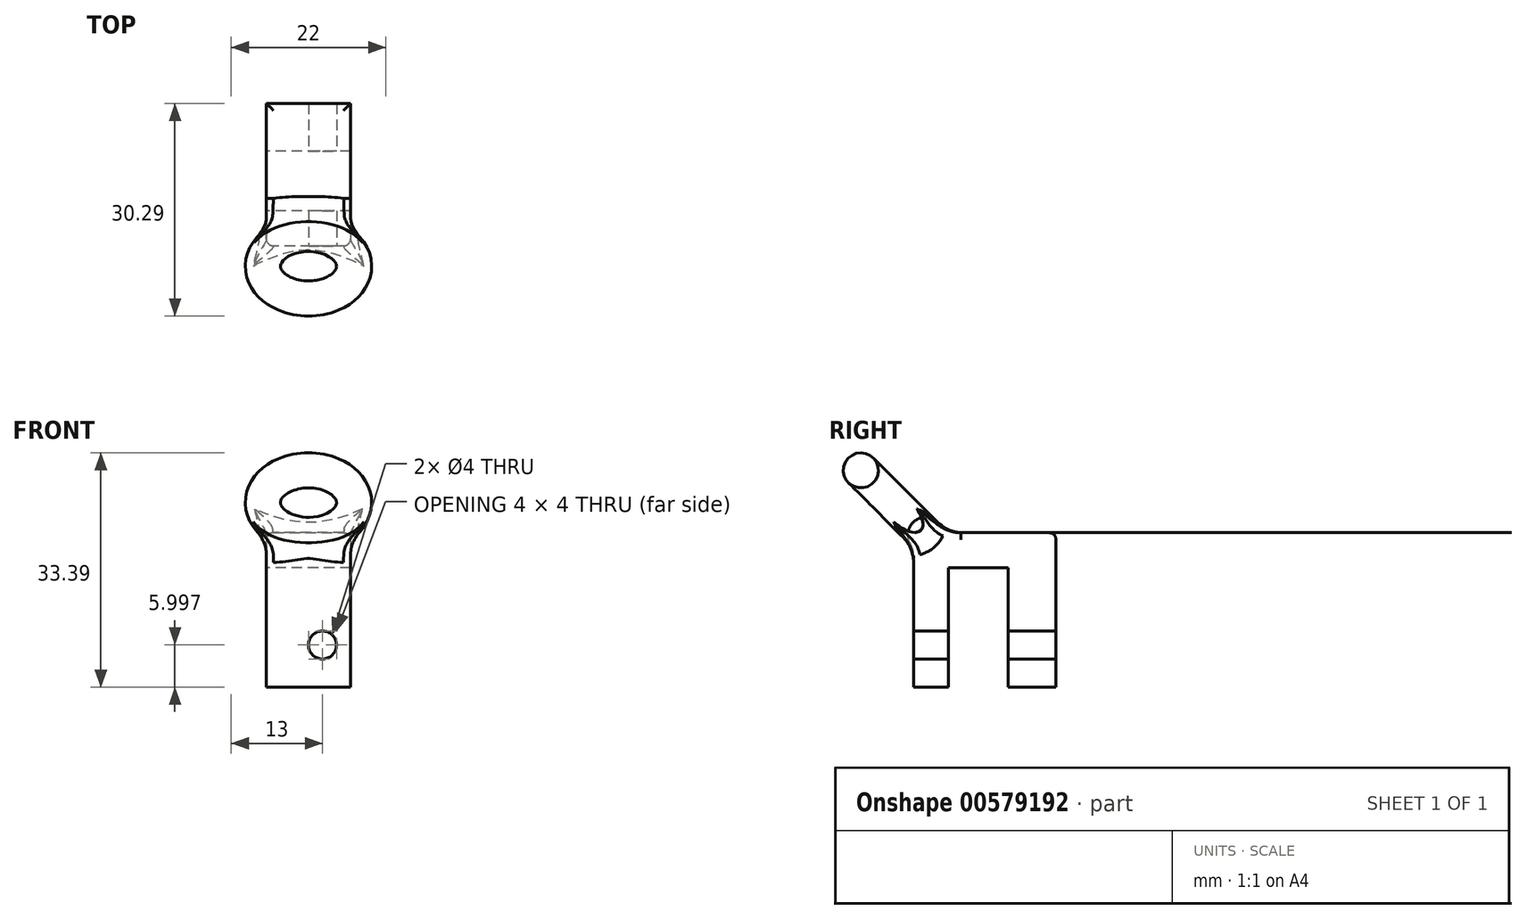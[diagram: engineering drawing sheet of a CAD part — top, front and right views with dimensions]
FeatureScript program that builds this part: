
annotation { "Feature Type Name" : "Feature", "Feature Type Description" : "" }
export const myFeature = defineFeature(function(context is Context, id is Id, definition is map)
    precondition{}
    {
        {
            var Q0;
            Q0=qCreatedBy(makeId("Right.planeOp"),FACE);
            var sketch = newSketch(context, id + "F0", { "sketchPlane" : qUnion([Q0])});
            skLineSegment(sketch, "E0", {"start": v(-9.26, -3.55) * mm, "end": v(-9.26, 18.45) * mm});
            skLineSegment(sketch, "E1", {"start": v(-9.26, 18.45) * mm, "end": v(11.04, 18.45) * mm});
            skLineSegment(sketch, "E2", {"start": v(11.04, 18.45) * mm, "end": v(11.04, -3.55) * mm});
            skLineSegment(sketch, "E3", {"start": v(11.04, -3.55) * mm, "end": v(4.24, -3.55) * mm});
            skLineSegment(sketch, "E4", {"start": v(4.24, -3.55) * mm, "end": v(4.24, 13.45) * mm});
            skLineSegment(sketch, "E5", {"start": v(4.24, 13.45) * mm, "end": v(-4.26, 13.45) * mm});
            skLineSegment(sketch, "E6", {"start": v(-4.26, 13.45) * mm, "end": v(-4.26, -3.55) * mm});
            skLineSegment(sketch, "E7", {"start": v(-4.26, -3.55) * mm, "end": v(-9.26, -3.55) * mm});
            skSolve(sketch);
        }
        {
            var Q0;
            Q0=makeQuery(id+"F0.imprint","IMPRINT",FACE,{"disambiguationData":[TD([[makeQuery(id+"F0.imprint","IMPRINT",EDGE,{"derivedFrom":sQuery(id+"F0.wireOp",EDGE,"E0")}),-1.0]])]});
            extrude(context, id + "F1", {"entities" : qUnion([Q0]), "endBound" : BoundingType.SYMMETRIC, "depth" : 12 * mm, "offsetDistance" : 25 * mm});
        }
        {
            var Q0;
            Q0=makeQuery(id+"F1.opExtrude","SWEPT_FACE",FACE,{"disambiguationData":[OSD([sQuery(id+"F0.wireOp",EDGE,"E0")])]});
            var sketch = newSketch(context, id + "F2", { "sketchPlane" : qUnion([Q0])});
            skPoint(sketch, "E8", {"position": v(2, 2.45) * mm});
            skSolve(sketch);
        }
        {
            var Q0;
            Q0=sQuery(id+"F2.wireOp",VERTEX,"E8");
            var Q1;
            Q1=makeQuery(id+"F1.opExtrude","SWEPT_BODY",BODY,{"disambiguationData":[OSD([sQuery(id+"F0.wireOp",EDGE,"E0"),sQuery(id+"F0.wireOp",EDGE,"E1"),sQuery(id+"F0.wireOp",EDGE,"E2"),sQuery(id+"F0.wireOp",EDGE,"E3"),sQuery(id+"F0.wireOp",EDGE,"E4"),sQuery(id+"F0.wireOp",EDGE,"E5"),sQuery(id+"F0.wireOp",EDGE,"E6"),sQuery(id+"F0.wireOp",EDGE,"E7")])]});
            hole(context, id + "F3", {"style" : HoleStyle.SIMPLE, "endStyle" : HoleEndStyle.THROUGH, "holeDiameter" : 4 * mm, "isTappedThrough" : true, "tappedDepth" : 12 * mm, "tapClearance" : 3, "locations" : qUnion([Q0]), "scope" : qUnion([Q1])});
        }
        {
            var Q0;
            Q0=makeQuery(id+"F1.opExtrude","SWEPT_FACE",FACE,{"disambiguationData":[OSD([sQuery(id+"F0.wireOp",EDGE,"E1")])]});
            var sketch = newSketch(context, id + "F4", { "sketchPlane" : qUnion([Q0])});
            skCircle(sketch, "E9", {"center": v(6.5, -3.17) * mm, "radius": 2.5 * mm});
            skLineSegment(sketch, "E10", {"start": v(0, -9.26) * mm, "end": v(0, 11.04) * mm});
            skSolve(sketch);
        }
        {
            var Q0;
            {var subQ0=sQuery(id+"F4.wireOp",EDGE,"E9");var subQ1=makeQuery(id+"F1.opExtrude","CAP_EDGE",EDGE,{"disambiguationData":[OSD([sQuery(id+"F0.wireOp",EDGE,"E1")])],"isStart":false});var subQ2=makeQuery(id+"F4.imprint","INTERSECT",VERTEX,{"disambiguationData":[OD(0.0)],"derivedFrom":[subQ1,subQ0]});Q0=makeQuery(id+"F4.imprint","IMPRINT",FACE,{"disambiguationData":[TD([[makeQuery(id+"F4.imprint","IMPRINT",EDGE,{"disambiguationData":[TD([[subQ2,-1.0]])],"derivedFrom":subQ0}),1.0]])]});}
            var Q1;
            {var subQ0=sQuery(id+"F4.wireOp",EDGE,"E9");var subQ1=makeQuery(id+"F1.opExtrude","CAP_EDGE",EDGE,{"disambiguationData":[OSD([sQuery(id+"F0.wireOp",EDGE,"E1")])],"isStart":false});var subQ2=makeQuery(id+"F4.imprint","INTERSECT",VERTEX,{"disambiguationData":[OD(0.0)],"derivedFrom":[subQ1,subQ0]});Q1=makeQuery(id+"F4.imprint","IMPRINT",FACE,{"disambiguationData":[TD([[makeQuery(id+"F4.imprint","IMPRINT",EDGE,{"disambiguationData":[TD([[subQ2,1.0]])],"derivedFrom":subQ0}),1.0]])]});}
            var Q2;
            Q2=sQuery(id+"F4.wireOp",EDGE,"E10");
            revolve(context, id + "F5", {"entities" : qUnion([Q0, Q1]), "axis" : qUnion([Q2]), "revolveType" : RevolveType.FULL});
        }
        {
            var Q0;
            Q0=makeQuery(id+"F5.opRevolve","SWEPT_BODY",BODY,{"disambiguationData":[OSD([sQuery(id+"F4.wireOp",EDGE,"E9")])]});
            var Q1;
            Q1=makeQuery(id+"F1.opExtrude","SWEPT_EDGE",EDGE,{"disambiguationData":[OSD([sQuery(id+"F0.wireOp",EDGE,"E0"),sQuery(id+"F0.wireOp",EDGE,"E1")])]});
            transform(context, id + "F6", {"entities" : qUnion([Q0]), "transformType" : TransformType.ROTATION, "transformAxis" : qUnion([Q1]), "angle" : 45 * degree, "oppositeDirection" : true, "makeCopy" : false});
        }
        {
            var Q0;
            Q0=makeQuery(id+"F5.opRevolve","SWEPT_BODY",BODY,{"disambiguationData":[OSD([sQuery(id+"F4.wireOp",EDGE,"E9")])]});
            var Q1;
            Q1=qCreatedBy(makeId("Front.planeOp"),FACE);
            transform(context, id + "F7", {"entities" : qUnion([Q0]), "transformType" : TransformType.TRANSLATION_DISTANCE, "transformDirection" : qUnion([Q1]), "distance" : 7.2 * mm, "makeCopy" : false});
        }
        {
            var Q0;
            Q0=makeQuery(id+"F5.opRevolve","SWEPT_BODY",BODY,{"disambiguationData":[OSD([sQuery(id+"F4.wireOp",EDGE,"E9")])]});
            var Q1;
            Q1=makeQuery(id+"F1.opExtrude","SWEPT_BODY",BODY,{"disambiguationData":[OSD([sQuery(id+"F0.wireOp",EDGE,"E0"),sQuery(id+"F0.wireOp",EDGE,"E1"),sQuery(id+"F0.wireOp",EDGE,"E2"),sQuery(id+"F0.wireOp",EDGE,"E3"),sQuery(id+"F0.wireOp",EDGE,"E4"),sQuery(id+"F0.wireOp",EDGE,"E5"),sQuery(id+"F0.wireOp",EDGE,"E6"),sQuery(id+"F0.wireOp",EDGE,"E7")])]});
            booleanBodies(context, id + "F8", {"operationType" : BooleanOperationType.UNION, "tools" : qUnion([Q0, Q1])});
        }
        {
            var Q0;
            Q0=makeQuery(id+"F8.opBoolean","INTERSECT",EDGE,{"derivedFrom":[makeQuery(id+"F1.opExtrude","SWEPT_FACE",FACE,{"disambiguationData":[OSD([sQuery(id+"F0.wireOp",EDGE,"E0")])]}),makeQuery(id+"F5.opRevolve","SWEPT_FACE",FACE,{"disambiguationData":[OSD([sQuery(id+"F4.wireOp",EDGE,"E9")])]})]});
            var Q1;
            Q1=makeQuery(id+"F8.opBoolean","INTERSECT",EDGE,{"derivedFrom":[makeQuery(id+"F1.opExtrude","SWEPT_FACE",FACE,{"disambiguationData":[OSD([sQuery(id+"F0.wireOp",EDGE,"E1")])]}),makeQuery(id+"F5.opRevolve","SWEPT_FACE",FACE,{"disambiguationData":[OSD([sQuery(id+"F4.wireOp",EDGE,"E9")])]})]});
            var Q2;
            Q2=makeQuery(id+"F8.opBoolean","INTERSECT",EDGE,{"derivedFrom":[makeQuery(id+"F1.opExtrude","CAP_FACE",FACE,{"disambiguationData":[OSD([sQuery(id+"F0.wireOp",EDGE,"E0"),sQuery(id+"F0.wireOp",EDGE,"E1"),sQuery(id+"F0.wireOp",EDGE,"E2"),sQuery(id+"F0.wireOp",EDGE,"E3"),sQuery(id+"F0.wireOp",EDGE,"E4"),sQuery(id+"F0.wireOp",EDGE,"E5"),sQuery(id+"F0.wireOp",EDGE,"E6"),sQuery(id+"F0.wireOp",EDGE,"E7")])],"isStart":false}),makeQuery(id+"F5.opRevolve","SWEPT_FACE",FACE,{"disambiguationData":[OSD([sQuery(id+"F4.wireOp",EDGE,"E9")])]})]});
            var Q3;
            Q3=makeQuery(id+"F8.opBoolean","INTERSECT",EDGE,{"derivedFrom":[makeQuery(id+"F1.opExtrude","CAP_FACE",FACE,{"disambiguationData":[OSD([sQuery(id+"F0.wireOp",EDGE,"E0"),sQuery(id+"F0.wireOp",EDGE,"E1"),sQuery(id+"F0.wireOp",EDGE,"E2"),sQuery(id+"F0.wireOp",EDGE,"E3"),sQuery(id+"F0.wireOp",EDGE,"E4"),sQuery(id+"F0.wireOp",EDGE,"E5"),sQuery(id+"F0.wireOp",EDGE,"E6"),sQuery(id+"F0.wireOp",EDGE,"E7")])],"isStart":true}),makeQuery(id+"F5.opRevolve","SWEPT_FACE",FACE,{"disambiguationData":[OSD([sQuery(id+"F4.wireOp",EDGE,"E9")])]})]});
            fillet(context, id + "F9", {"entities" : qUnion([Q0, Q1, Q2, Q3]), "radius" : 5 * mm, "tangentPropagation" : true, "allowEdgeOverflow" : false});
        }
        {
            var Q0;
            Q0=makeQuery(id+"F1.opExtrude","CAP_EDGE",EDGE,{"disambiguationData":[OSD([sQuery(id+"F0.wireOp",EDGE,"E1")])],"isStart":false});
            var Q1;
            Q1=makeQuery(id+"F1.opExtrude","CAP_EDGE",EDGE,{"disambiguationData":[OSD([sQuery(id+"F0.wireOp",EDGE,"E1")])],"isStart":true});
            var Q2;
            Q2=makeQuery(id+"F1.opExtrude","SWEPT_EDGE",EDGE,{"disambiguationData":[OSD([sQuery(id+"F0.wireOp",EDGE,"E1"),sQuery(id+"F0.wireOp",EDGE,"E2")])]});
            var Q3;
            Q3=makeQuery(id+"F1.opExtrude","CAP_EDGE",EDGE,{"disambiguationData":[OSD([sQuery(id+"F0.wireOp",EDGE,"E0")])],"isStart":false});
            var Q4;
            Q4=makeQuery(id+"F1.opExtrude","CAP_EDGE",EDGE,{"disambiguationData":[OSD([sQuery(id+"F0.wireOp",EDGE,"E0")])],"isStart":true});
            fillet(context, id + "F10", {"entities" : qUnion([Q0, Q1, Q2, Q3, Q4]), "radius" : 1 * mm, "tangentPropagation" : true, "allowEdgeOverflow" : false});
        }
    });
